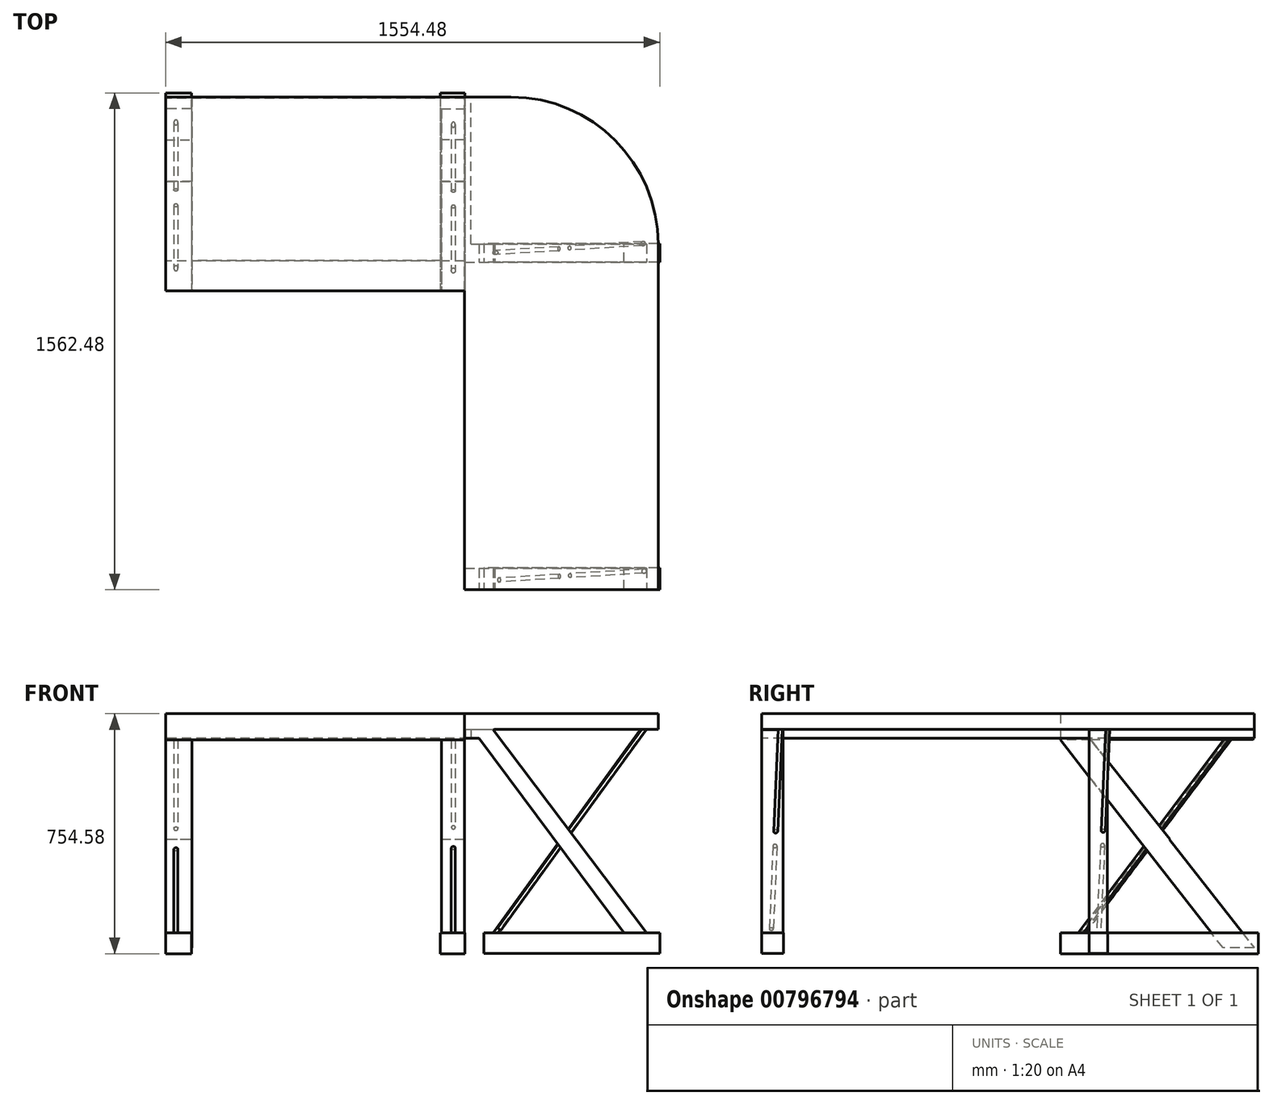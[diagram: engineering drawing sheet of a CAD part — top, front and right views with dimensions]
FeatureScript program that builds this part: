
annotation { "Feature Type Name" : "Feature", "Feature Type Description" : "" }
export const myFeature = defineFeature(function(context is Context, id is Id, definition is map)
    precondition{}
    {
        {
            var Q0;
            Q0=qCreatedBy(makeId("Top.planeOp"),FACE);
            var sketch = newSketch(context, id + "F0", { "sketchPlane" : qUnion([Q0])});
            skLineSegment(sketch, "E0.bottom", {"start": v(0, 0) * mm, "end": v(939.8, 0) * mm});
            skLineSegment(sketch, "E0.top", {"start": v(0, 609.6) * mm, "end": v(939.8, 609.6) * mm});
            skLineSegment(sketch, "E0.left", {"start": v(0, 0) * mm, "end": v(0, 609.6) * mm});
            skLineSegment(sketch, "E1.bottom", {"start": v(939.8, 609.6) * mm, "end": v(1086.87, 609.6) * mm});
            skLineSegment(sketch, "E1.top", {"start": v(939.8, -939.8) * mm, "end": v(1549.4, -939.8) * mm});
            skLineSegment(sketch, "E1.left", {"start": v(939.8, 0) * mm, "end": v(939.8, -939.8) * mm});
            skLineSegment(sketch, "E1.right", {"start": v(1549.4, 147.07) * mm, "end": v(1549.4, -939.8) * mm});
            skPoint(sketch, "E2.visualSharp", {"position": v(1549.4, 609.6) * mm});
            skArc(sketch, "E2.filletArc", {"start": v(1549.4, 147.07) * mm, "mid": v(1413.93, 474.13) * mm, "end": v(1086.87, 609.6) * mm});
            skSolve(sketch);
        }
        {
            var Q0;
            Q0=makeQuery(id+"F0.imprint","IMPRINT",FACE,{"disambiguationData":[TD([[makeQuery(id+"F0.imprint","IMPRINT",EDGE,{"derivedFrom":sQuery(id+"F0.wireOp",EDGE,"E0.bottom")}),1.0]])]});
            extrude(context, id + "F1", {"entities" : qUnion([Q0]), "depth" : 736.6 * mm, "offsetDistance" : 25.4 * mm});
        }
        {
            var Q0;
            Q0=makeQuery(id+"F1.opExtrude","SWEPT_FACE",FACE,{"disambiguationData":[OSD([sQuery(id+"F0.wireOp",EDGE,"E1.top")])]});
            var sketch = newSketch(context, id + "F2", { "sketchPlane" : qUnion([Q0])});
            skLineSegment(sketch, "E3", {"start": v(1549.4, 688.16) * mm, "end": v(1031.06, 686.32) * mm});
            skLineSegment(sketch, "E4", {"start": v(1031.06, 686.32) * mm, "end": v(1549.4, 0) * mm});
            skLineSegment(sketch, "E5", {"start": v(1549.4, 0) * mm, "end": v(1549.4, 688.16) * mm});
            skSolve(sketch);
        }
        {
            var Q0;
            Q0 = qSketchRegion(id + "F2", true);
            extrude(context, id + "F3", {"entities" : qUnion([Q0]), "operationType" : NewBodyOperationType.REMOVE, "oppositeDirection" : true, "depth" : 1587.5 * mm, "offsetDistance" : 25.4 * mm});
        }
        {
            var Q0;
            Q0=makeQuery(id+"F1.opExtrude","SWEPT_FACE",FACE,{"disambiguationData":[OSD([sQuery(id+"F0.wireOp",EDGE,"E1.top")])]});
            var sketch = newSketch(context, id + "F4", { "sketchPlane" : qUnion([Q0])});
            skLineSegment(sketch, "E6", {"start": v(1463.76, 0) * mm, "end": v(1250.86, 281.9) * mm});
            skLineSegment(sketch, "E7", {"start": v(1250.86, 281.9) * mm, "end": v(1044.16, 0) * mm});
            skLineSegment(sketch, "E8", {"start": v(1044.16, 0) * mm, "end": v(1463.76, 0) * mm});
            skSolve(sketch);
        }
        {
            var Q0;
            Q0=makeQuery(id+"F4.imprint","IMPRINT",FACE,{"disambiguationData":[TD([[makeQuery(id+"F4.imprint","IMPRINT",EDGE,{"derivedFrom":sQuery(id+"F4.wireOp",EDGE,"E6")}),1.0]])]});
            extrude(context, id + "F5", {"entities" : qUnion([Q0]), "operationType" : NewBodyOperationType.REMOVE, "oppositeDirection" : true, "depth" : 1803.4 * mm, "offsetDistance" : 25.4 * mm});
        }
        {
            var Q0;
            Q0=makeQuery(id+"F1.opExtrude","SWEPT_FACE",FACE,{"disambiguationData":[OSD([sQuery(id+"F0.wireOp",EDGE,"E1.top")])]});
            var sketch = newSketch(context, id + "F6", { "sketchPlane" : qUnion([Q0])});
            skLineSegment(sketch, "E9", {"start": v(1478.3, 0) * mm, "end": v(986.02, 659.28) * mm});
            skLineSegment(sketch, "E10", {"start": v(986.02, 659.28) * mm, "end": v(939.8, 659.28) * mm});
            skLineSegment(sketch, "E11", {"start": v(939.8, 659.28) * mm, "end": v(939.8, 0) * mm});
            skLineSegment(sketch, "E12", {"start": v(939.8, 0) * mm, "end": v(1478.3, 0) * mm});
            skSolve(sketch);
        }
        {
            var Q0;
            Q0 = qSketchRegion(id + "F6", true);
            extrude(context, id + "F7", {"entities" : qUnion([Q0]), "operationType" : NewBodyOperationType.REMOVE, "oppositeDirection" : true, "depth" : 2174.24 * mm, "offsetDistance" : 25.4 * mm});
        }
        {
            var Q0;
            Q0=makeQuery(id+"F1.opExtrude","SWEPT_FACE",FACE,{"disambiguationData":[OSD([sQuery(id+"F0.wireOp",EDGE,"E1.top")])]});
            var sketch = newSketch(context, id + "F8", { "sketchPlane" : qUnion([Q0])});
            skLineSegment(sketch, "E13", {"start": v(1304.07, 324.83) * mm, "end": v(1549.4, 688.16) * mm});
            skLineSegment(sketch, "E14", {"start": v(1549.4, 688.16) * mm, "end": v(1034.76, 688.16) * mm});
            skLineSegment(sketch, "E15", {"start": v(1034.76, 688.16) * mm, "end": v(1304.07, 324.83) * mm});
            skSolve(sketch);
        }
        {
            var Q0;
            Q0 = qSketchRegion(id + "F8", true);
            extrude(context, id + "F9", {"entities" : qUnion([Q0]), "operationType" : NewBodyOperationType.REMOVE, "oppositeDirection" : true, "depth" : 1635.76 * mm, "offsetDistance" : 25.4 * mm});
        }
        {
            var Q0;
            Q0=makeQuery(id+"F1.opExtrude","SWEPT_FACE",FACE,{"disambiguationData":[OSD([sQuery(id+"F0.wireOp",EDGE,"E0.left")])]});
            var sketch = newSketch(context, id + "F10", { "sketchPlane" : qUnion([Q0])});
            skLineSegment(sketch, "E16", {"start": v(-623.32, 676.57) * mm, "end": v(-32.98, -30.91) * mm, "construction": true});
            skLineSegment(sketch, "E17", {"start": v(-572.46, 713.56) * mm, "end": v(89.95, -80.3) * mm, "construction": true});
            skLineSegment(sketch, "E18", {"start": v(-624.86, -21.66) * mm, "end": v(-99.26, 653.45) * mm, "construction": true});
            skLineSegment(sketch, "E19", {"start": v(-12.95, 641.12) * mm, "end": v(-528, -20.45) * mm, "construction": true});
            skLineSegment(sketch, "E20", {"start": v(-609.6, 660.13) * mm, "end": v(-609.6, 0) * mm});
            skLineSegment(sketch, "E21", {"start": v(-609.6, 0) * mm, "end": v(-343.73, 341.5) * mm});
            skLineSegment(sketch, "E22", {"start": v(-343.73, 341.5) * mm, "end": v(-609.6, 660.13) * mm});
            skSolve(sketch);
        }
        {
            var Q0;
            Q0=makeQuery(id+"F10.imprint","IMPRINT",FACE,{"disambiguationData":[TD([[makeQuery(id+"F10.imprint","IMPRINT",EDGE,{"derivedFrom":sQuery(id+"F10.wireOp",EDGE,"E20")}),1.0]])]});
            extrude(context, id + "F11", {"entities" : qUnion([Q0]), "operationType" : NewBodyOperationType.REMOVE, "oppositeDirection" : true, "depth" : 955.04 * mm, "offsetDistance" : 25.4 * mm});
        }
        {
            var Q0;
            Q0=makeQuery(id+"F10.imprint","IMPRINT",FACE,{"disambiguationData":[TD([[makeQuery(id+"F10.imprint","IMPRINT",EDGE,{"derivedFrom":sQuery(id+"F10.wireOp",EDGE,"E21")}),-1.0]])]});
            var sketch = newSketch(context, id + "F12", { "sketchPlane" : qUnion([Q0])});
            skLineSegment(sketch, "E23", {"start": v(-94.48, 656.07) * mm, "end": v(-606.15, 656.07) * mm});
            skLineSegment(sketch, "E24", {"start": v(-606.15, 656.07) * mm, "end": v(-362.59, 318.86) * mm});
            skLineSegment(sketch, "E25", {"start": v(-362.59, 318.86) * mm, "end": v(-94.48, 656.07) * mm});
            skSolve(sketch);
        }
        {
            var Q0;
            Q0 = qSketchRegion(id + "F12", true);
            extrude(context, id + "F13", {"entities" : qUnion([Q0]), "operationType" : NewBodyOperationType.REMOVE, "oppositeDirection" : true, "depth" : 949.96 * mm, "offsetDistance" : 25.4 * mm});
        }
        {
            var Q0;
            Q0=makeQuery(id+"F10.imprint","IMPRINT",FACE,{"disambiguationData":[TD([[makeQuery(id+"F10.imprint","IMPRINT",EDGE,{"derivedFrom":sQuery(id+"F10.wireOp",EDGE,"E21")}),-1.0]])]});
            var sketch = newSketch(context, id + "F14", { "sketchPlane" : qUnion([Q0])});
            skLineSegment(sketch, "E26", {"start": v(0, 654.22) * mm, "end": v(-511.63, 0) * mm});
            skLineSegment(sketch, "E27", {"start": v(-511.63, 0) * mm, "end": v(0, 0) * mm});
            skLineSegment(sketch, "E28", {"start": v(0, 0) * mm, "end": v(0, 654.22) * mm});
            skSolve(sketch);
        }
        {
            var Q0;
            Q0=makeQuery(id+"F14.imprint","IMPRINT",FACE,{"disambiguationData":[TD([[makeQuery(id+"F14.imprint","IMPRINT",EDGE,{"derivedFrom":sQuery(id+"F14.wireOp",EDGE,"E26")}),1.0]])]});
            extrude(context, id + "F15", {"entities" : qUnion([Q0]), "operationType" : NewBodyOperationType.REMOVE, "oppositeDirection" : true, "depth" : 944.88 * mm, "offsetDistance" : 25.4 * mm});
        }
        {
            var Q0;
            Q0=makeQuery(id+"F1.opExtrude","SWEPT_FACE",FACE,{"disambiguationData":[OSD([sQuery(id+"F0.wireOp",EDGE,"E0.bottom")])]});
            var sketch = newSketch(context, id + "F16", { "sketchPlane" : qUnion([Q0])});
            skLineSegment(sketch, "E29.bottom", {"start": v(82.98, 654.22) * mm, "end": v(867.72, 654.22) * mm});
            skLineSegment(sketch, "E29.top", {"start": v(82.98, 0) * mm, "end": v(867.72, 0) * mm});
            skLineSegment(sketch, "E29.left", {"start": v(82.98, 654.22) * mm, "end": v(82.98, 0) * mm});
            skLineSegment(sketch, "E29.right", {"start": v(867.72, 654.22) * mm, "end": v(867.72, 0) * mm});
            skSolve(sketch);
        }
        {
            var Q0;
            Q0 = qSketchRegion(id + "F16", true);
            extrude(context, id + "F17", {"entities" : qUnion([Q0]), "operationType" : NewBodyOperationType.REMOVE, "oppositeDirection" : true, "depth" : 627.38 * mm, "offsetDistance" : 25.4 * mm});
        }
        {
            var Q0;
            Q0=makeQuery(id+"F1.opExtrude","SWEPT_FACE",FACE,{"disambiguationData":[OSD([sQuery(id+"F0.wireOp",EDGE,"E1.right")])]});
            var sketch = newSketch(context, id + "F18", { "sketchPlane" : qUnion([Q0])});
            skLineSegment(sketch, "E30.bottom", {"start": v(-872.65, 688.16) * mm, "end": v(90.82, 688.16) * mm});
            skLineSegment(sketch, "E30.top", {"start": v(-872.65, 0) * mm, "end": v(90.82, 0) * mm});
            skLineSegment(sketch, "E30.left", {"start": v(-872.65, 688.16) * mm, "end": v(-872.65, 0) * mm});
            skLineSegment(sketch, "E30.right", {"start": v(90.82, 688.16) * mm, "end": v(90.82, 0) * mm});
            skSolve(sketch);
        }
        {
            var Q0;
            Q0 = qSketchRegion(id + "F18", true);
            extrude(context, id + "F19", {"entities" : qUnion([Q0]), "operationType" : NewBodyOperationType.REMOVE, "oppositeDirection" : true, "depth" : 607.06 * mm, "offsetDistance" : 25.4 * mm});
        }
        {
            var Q0;
            Q0=makeQuery(id+"F1.opExtrude","SWEPT_FACE",FACE,{"disambiguationData":[OSD([sQuery(id+"F0.wireOp",EDGE,"E1.right")])]});
            var sketch = newSketch(context, id + "F20", { "sketchPlane" : qUnion([Q0])});
            skLineSegment(sketch, "E31.bottom", {"start": v(147.07, 688.16) * mm, "end": v(618.34, 688.16) * mm});
            skLineSegment(sketch, "E31.top", {"start": v(147.07, 0) * mm, "end": v(618.34, 0) * mm});
            skLineSegment(sketch, "E31.left", {"start": v(147.07, 688.16) * mm, "end": v(147.07, 0) * mm});
            skLineSegment(sketch, "E31.right", {"start": v(618.34, 688.16) * mm, "end": v(618.34, 0) * mm});
            skSolve(sketch);
        }
        {
            var Q0;
            Q0 = qSketchRegion(id + "F20", true);
            extrude(context, id + "F21", {"entities" : qUnion([Q0]), "operationType" : NewBodyOperationType.REMOVE, "oppositeDirection" : true, "depth" : 589.28 * mm, "offsetDistance" : 25.4 * mm});
        }
        {
            var Q0;
            Q0=qCreatedBy(makeId("Top.planeOp"),FACE);
            cPlane(context, id + "F22", {"entities" : qUnion([Q0]), "cplaneType" : CPlaneType.OFFSET, "offset" : 25.4 * mm, "width" : 152.4 * mm, "height" : 152.4 * mm});
        }
        {
            var Q0;
            Q0=qCreatedBy(id+"F22.planeOp",FACE);
            var sketch = newSketch(context, id + "F23", { "sketchPlane" : qUnion([Q0])});
            skLineSegment(sketch, "E32", {"start": v(0, -21.67) * mm, "end": v(-153.97, -21.67) * mm, "construction": true});
            skSolve(sketch);
        }
        {
            var Q0;
            Q0=sQuery(id+"F23.wireOp",EDGE,"E32");
            cPlane(context, id + "F24", {"entities" : qUnion([Q0]), "cplaneType" : CPlaneType.LINE_ANGLE, "offset" : 25.4 * mm, "angle" : 127 * degree, "width" : 152.4 * mm, "height" : 152.4 * mm});
        }
        {
            var Q0;
            Q0=qCreatedBy(id+"F24.planeOp",FACE);
            var sketch = newSketch(context, id + "F25", { "sketchPlane" : qUnion([Q0])});
            skCircle(sketch, "E33", {"center": v(32.65, 28.3) * mm, "radius": 6.35 * mm});
            skCircle(sketch, "E34", {"center": v(905.35, 22.65) * mm, "radius": 6.35 * mm});
            skSolve(sketch);
        }
        {
            var Q0;
            Q0=makeQuery(id+"F25.imprint","IMPRINT",FACE,{"disambiguationData":[TD([[makeQuery(id+"F25.imprint","IMPRINT",EDGE,{"derivedFrom":sQuery(id+"F25.wireOp",EDGE,"E33")}),1.0]])]});
            var Q1;
            Q1=makeQuery(id+"F25.imprint","IMPRINT",FACE,{"disambiguationData":[TD([[makeQuery(id+"F25.imprint","IMPRINT",EDGE,{"derivedFrom":sQuery(id+"F25.wireOp",EDGE,"E34")}),1.0]])]});
            extrude(context, id + "F26", {"entities" : qUnion([Q0, Q1]), "operationType" : NewBodyOperationType.ADD, "depth" : 899.16 * mm, "offsetDistance" : 25.4 * mm});
        }
        {
            var Q0;
            Q0=qCreatedBy(id+"F22.planeOp",FACE);
            var sketch = newSketch(context, id + "F27", { "sketchPlane" : qUnion([Q0])});
            skLineSegment(sketch, "E35", {"start": v(1029.39, 183.9) * mm, "end": v(1040.64, 0) * mm, "construction": true});
            skSolve(sketch);
        }
        {
            var Q0;
            Q0=sQuery(id+"F27.wireOp",EDGE,"E35");
            cPlane(context, id + "F28", {"entities" : qUnion([Q0]), "cplaneType" : CPlaneType.LINE_ANGLE, "offset" : 25.4 * mm, "angle" : 144 * degree, "width" : 152.4 * mm, "height" : 152.4 * mm});
        }
        {
            var Q0;
            Q0=qCreatedBy(id+"F28.planeOp",FACE);
            var sketch = newSketch(context, id + "F29", { "sketchPlane" : qUnion([Q0])});
            skCircle(sketch, "E36", {"center": v(809.22, 118.2) * mm, "radius": 6.35 * mm});
            skPoint(sketch, "E37.center.orphan", {"position": v(0, -865.83) * mm});
            skCircle(sketch, "E38", {"center": v(838.45, -911.02) * mm, "radius": 6.3 * mm});
            skSolve(sketch);
        }
        {
            var Q0;
            Q0 = qSketchRegion(id + "F29", true);
            extrude(context, id + "F30", {"entities" : qUnion([Q0]), "operationType" : NewBodyOperationType.ADD, "depth" : 822.96 * mm, "offsetDistance" : 25.4 * mm});
        }
        {
            var Q0;
            Q0=qCreatedBy(makeId("Front.planeOp"),FACE);
            var sketch = newSketch(context, id + "F31", { "sketchPlane" : qUnion([Q0])});
            skLineSegment(sketch, "E39.bottom", {"start": v(81.2, 47.41) * mm, "end": v(0, 47.41) * mm});
            skLineSegment(sketch, "E39.top", {"start": v(81.2, -17.98) * mm, "end": v(0, -17.98) * mm});
            skLineSegment(sketch, "E39.left", {"start": v(81.2, 47.41) * mm, "end": v(81.2, -17.98) * mm});
            skLineSegment(sketch, "E39.right", {"start": v(0, 47.41) * mm, "end": v(0, -17.98) * mm});
            skLineSegment(sketch, "E40.bottom", {"start": v(864.69, 47.41) * mm, "end": v(940.98, 47.41) * mm});
            skLineSegment(sketch, "E40.top", {"start": v(864.69, -17.98) * mm, "end": v(940.98, -17.98) * mm});
            skLineSegment(sketch, "E40.left", {"start": v(864.69, 47.41) * mm, "end": v(864.69, -17.98) * mm});
            skLineSegment(sketch, "E40.right", {"start": v(940.98, 47.41) * mm, "end": v(940.98, -17.98) * mm});
            skSolve(sketch);
        }
        {
            var Q0;
            Q0 = qSketchRegion(id + "F31", true);
            extrude(context, id + "F32", {"entities" : qUnion([Q0]), "operationType" : NewBodyOperationType.ADD, "oppositeDirection" : true, "depth" : 622.3 * mm, "offsetDistance" : 25.4 * mm});
        }
        {
            var Q0;
            Q0=qCreatedBy(makeId("Right.planeOp"),FACE);
            cPlane(context, id + "F33", {"entities" : qUnion([Q0]), "cplaneType" : CPlaneType.OFFSET, "offset" : 1000.76 * mm, "width" : 152.4 * mm, "height" : 152.4 * mm});
        }
        {
            var Q0;
            Q0=qCreatedBy(id+"F33.planeOp",FACE);
            var sketch = newSketch(context, id + "F34", { "sketchPlane" : qUnion([Q0])});
            skLineSegment(sketch, "E41.bottom", {"start": v(149.26, 47.9) * mm, "end": v(90.12, 47.9) * mm});
            skLineSegment(sketch, "E41.top", {"start": v(149.26, -17.15) * mm, "end": v(90.12, -17.15) * mm});
            skLineSegment(sketch, "E41.left", {"start": v(149.26, 47.9) * mm, "end": v(149.26, -17.15) * mm});
            skLineSegment(sketch, "E41.right", {"start": v(90.12, 47.9) * mm, "end": v(90.12, -17.15) * mm});
            skLineSegment(sketch, "E42.bottom", {"start": v(-871.57, 47.9) * mm, "end": v(-940.18, 47.9) * mm});
            skLineSegment(sketch, "E42.top", {"start": v(-871.57, -17.15) * mm, "end": v(-940.18, -17.15) * mm});
            skLineSegment(sketch, "E42.left", {"start": v(-871.57, 47.9) * mm, "end": v(-871.57, -17.15) * mm});
            skLineSegment(sketch, "E42.right", {"start": v(-940.18, 47.9) * mm, "end": v(-940.18, -17.15) * mm});
            skSolve(sketch);
        }
        {
            var Q0;
            Q0=makeQuery(id+"F34.imprint","IMPRINT",FACE,{"disambiguationData":[TD([[makeQuery(id+"F34.imprint","IMPRINT",EDGE,{"derivedFrom":sQuery(id+"F34.wireOp",EDGE,"E42.bottom")}),1.0]])]});
            var Q1;
            Q1=makeQuery(id+"F34.imprint","IMPRINT",FACE,{"disambiguationData":[TD([[makeQuery(id+"F34.imprint","IMPRINT",EDGE,{"derivedFrom":sQuery(id+"F34.wireOp",EDGE,"E41.bottom")}),1.0]])]});
            extrude(context, id + "F35", {"entities" : qUnion([Q0, Q1]), "operationType" : NewBodyOperationType.ADD, "depth" : 553.72 * mm, "offsetDistance" : 25.4 * mm});
        }
    });
